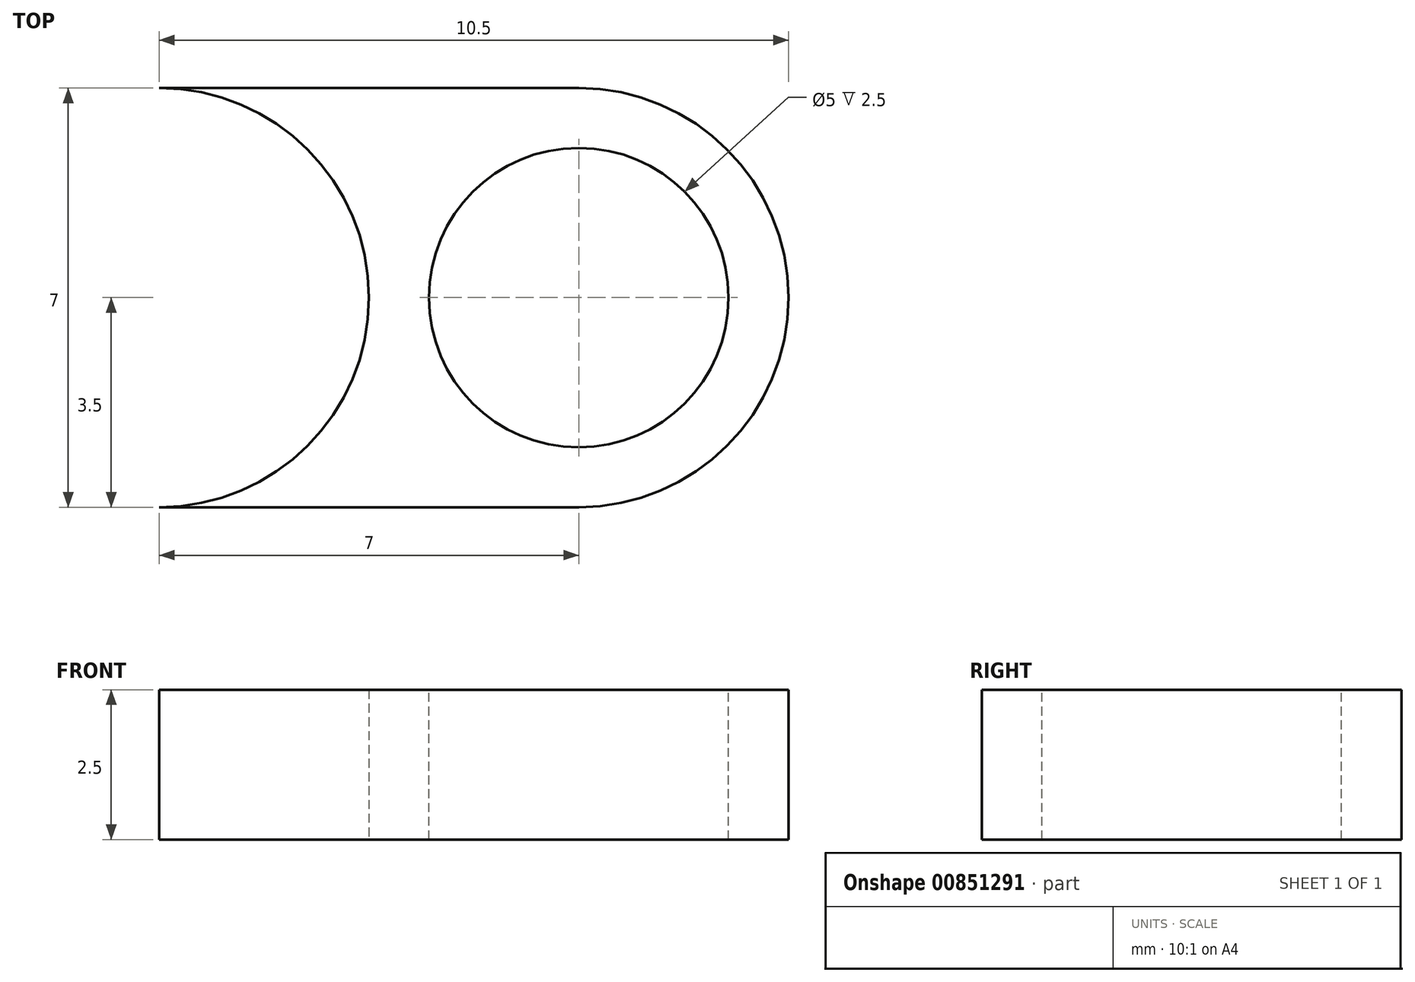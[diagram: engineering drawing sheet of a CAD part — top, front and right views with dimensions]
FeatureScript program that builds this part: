
annotation { "Feature Type Name" : "Feature", "Feature Type Description" : "" }
export const myFeature = defineFeature(function(context is Context, id is Id, definition is map)
    precondition{}
    {
        {
            var Q0;
            Q0=qCreatedBy(makeId("Top.planeOp"),FACE);
            var sketch = newSketch(context, id + "F0", { "sketchPlane" : qUnion([Q0])});
            skCircle(sketch, "E0", {"center": v(3.5, 0) * mm, "radius": 3.5 * mm});
            skLineSegment(sketch, "E1.bottom", {"start": v(3.5, 3.5) * mm, "end": v(0, 3.5) * mm});
            skLineSegment(sketch, "E1.top", {"start": v(3.5, -3.5) * mm, "end": v(0, -3.5) * mm});
            skLineSegment(sketch, "E1.left", {"start": v(3.5, 3.5) * mm, "end": v(3.5, -3.5) * mm});
            skLineSegment(sketch, "E1.right", {"start": v(0, 3.5) * mm, "end": v(0, -3.5) * mm});
            skLineSegment(sketch, "E2.MirrorCS", {"start": v(-3.5, 3.5) * mm, "end": v(0, 3.5) * mm});
            skLineSegment(sketch, "E3.MirrorCS", {"start": v(-3.5, -3.5) * mm, "end": v(0, -3.5) * mm});
            skCircle(sketch, "E4.MirrorC", {"center": v(-3.5, 0) * mm, "radius": 3.5 * mm});
            skPoint(sketch, "E5", {"position": v(-7, 0) * mm});
            skSolve(sketch);
        }
        {
            var Q0;
            {var subQ0=sQuery(id+"F0.wireOp",EDGE,"E1.left");Q0=makeQuery(id+"F0.imprint","IMPRINT",FACE,{"disambiguationData":[TD([[makeQuery(id+"F0.imprint","IMPRINT",EDGE,{"derivedFrom":subQ0}),1.0]])]});}
            var Q1;
            {var subQ0=sQuery(id+"F0.wireOp",EDGE,"E4.MirrorC");var subQ1=makeQuery(id+"F0.imprint","INTERSECT",VERTEX,{"derivedFrom":[sQuery(id+"F0.wireOp",EDGE,"E2.MirrorCS"),subQ0]});Q1=makeQuery(id+"F0.imprint","IMPRINT",FACE,{"disambiguationData":[TD([[makeQuery(id+"F0.imprint","IMPRINT",EDGE,{"disambiguationData":[TD([[subQ1,-1.0]])],"derivedFrom":subQ0}),-1.0]])]});}
            var Q2;
            {var subQ1=sQuery(id+"F0.wireOp",EDGE,"E1.bottom");Q2=makeQuery(id+"F0.imprint","IMPRINT",FACE,{"disambiguationData":[TD([[makeQuery(id+"F0.imprint","IMPRINT",EDGE,{"derivedFrom":subQ1}),1.0]])]});}
            var Q3;
            {var subQ0=sQuery(id+"F0.wireOp",EDGE,"E1.left");Q3=makeQuery(id+"F0.imprint","IMPRINT",FACE,{"disambiguationData":[TD([[makeQuery(id+"F0.imprint","IMPRINT",EDGE,{"derivedFrom":subQ0}),-1.0]])]});}
            var Q4;
            Q4=makeQuery(id+"F0.imprint","IMPRINT",FACE,{"disambiguationData":[TD([[makeQuery(id+"F0.imprint","IMPRINT",EDGE,{"derivedFrom":sQuery(id+"F0.wireOp",EDGE,"E1.right")}),-1.0]])]});
            var Q5;
            {var subQ0=sQuery(id+"F0.wireOp",EDGE,"E1.top");Q5=makeQuery(id+"F0.imprint","IMPRINT",FACE,{"disambiguationData":[TD([[makeQuery(id+"F0.imprint","IMPRINT",EDGE,{"derivedFrom":subQ0}),-1.0]])]});}
            extrude(context, id + "F1", {"entities" : qUnion([Q0, Q1, Q2, Q3, Q4, Q5]), "depth" : 2.5 * mm, "offsetDistance" : 25 * mm});
        }
        {
            var Q0;
            Q0=makeQuery(id+"F1.opExtrude","CAP_FACE",FACE,{"disambiguationData":[OSD([sQuery(id+"F0.wireOp",EDGE,"E0"),sQuery(id+"F0.wireOp",EDGE,"E1.bottom"),sQuery(id+"F0.wireOp",EDGE,"E1.top"),sQuery(id+"F0.wireOp",EDGE,"E2.MirrorCS"),sQuery(id+"F0.wireOp",EDGE,"E3.MirrorCS"),sQuery(id+"F0.wireOp",EDGE,"E4.MirrorC")])],"isStart":false});
            var sketch = newSketch(context, id + "F2", { "sketchPlane" : qUnion([Q0])});
            skCircle(sketch, "E6", {"center": v(-3.5, 0) * mm, "radius": 2.5 * mm});
            skCircle(sketch, "E7", {"center": v(3.5, 0) * mm, "radius": 2.5 * mm});
            skSolve(sketch);
        }
        {
            var Q0;
            Q0=makeQuery(id+"F2.imprint","IMPRINT",FACE,{"disambiguationData":[TD([[makeQuery(id+"F2.imprint","IMPRINT",EDGE,{"derivedFrom":sQuery(id+"F2.wireOp",EDGE,"E6")}),1.0]])]});
            var Q1;
            Q1=makeQuery(id+"F2.imprint","IMPRINT",FACE,{"disambiguationData":[TD([[makeQuery(id+"F2.imprint","IMPRINT",EDGE,{"derivedFrom":sQuery(id+"F2.wireOp",EDGE,"E7")}),1.0]])]});
            extrude(context, id + "F3", {"entities" : qUnion([Q0, Q1]), "operationType" : NewBodyOperationType.REMOVE, "oppositeDirection" : true, "depth" : 25 * mm, "offsetDistance" : 25 * mm});
        }
    });
